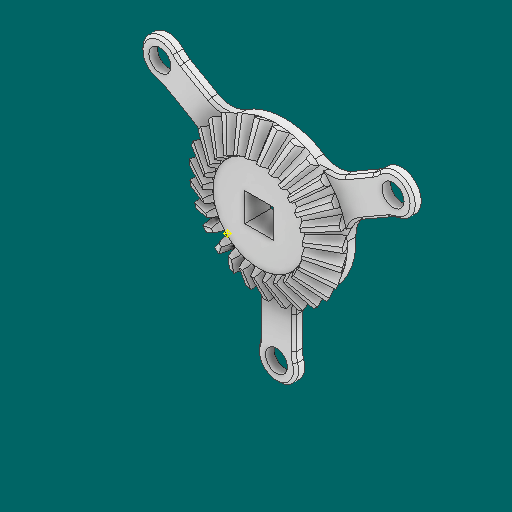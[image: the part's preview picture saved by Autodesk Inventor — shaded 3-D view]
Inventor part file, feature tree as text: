
AUTODESK INVENTOR PART (.ipt)
format: ipt  version: 2023.1 (Build 271208000, 208)  size: 768,512 bytes
history: native  units: mm
features: other x24, pattern_circular x3, sketch x3, loft x2, extrude x2, fillet x1, chamfer x1
ambient origin geometry x6: Origin, XZ Plane, X Axis, Y Axis, Z Axis, Center Point
bodies: Solid1 (feature_tree)
feature tree (36):
  other  "Top Point"
  other  "Mesh Plane2"
  other  "Teeth Body"
  other  "Start Point"
  other  "Tooth Plane"
  other  "Start Sketch"
  other  "End Point"
  other  "3D Sketch Right"
  other  "End Plane Right"
  loft  "Loft Right"
  pattern_circular  "Circular Pattern Right"  [2 undecoded]
  other  "3D Sketch Left"
  other  "End Plane Left"
  loft  "Loft Left"
  pattern_circular  "Circular Pattern Left"  [2 undecoded]
  other  "Fix Body"
  extrude  "Extrusion1"  Depth=5.08mm
  fillet  "Fillet1"  Radius=31.06566mm
  pattern_circular  "Circular Pattern4"  [2 undecoded]
  extrude  "Extrusion2"  Depth=5.08mm
  chamfer  "Chamfer1"  Distance=6.192895mm
  other  "Mesh Plane"
  other  "Top Plane"
  other  "Teeth Body Sketch"
  other  "End Plane"
  other  "End Sketch"
  other  "Helical Curve Left"
  other  "End Sketch Left"
  other  "Body Sketch"
  sketch  "Sketch6"  dims[d0=34.29mm d1=32.736122mm]
  other  "Srf1"
  other  "Helical Curve Right"
  other  "End Sketch Right"
  sketch  "Sketch8"  dims[d2=35.584898mm]
  sketch  "Sketch9"  dims[d3=6.985mm d4=9.06743mm d5=90.0deg d7=9.009874mm d8=9.638731mm d9=31.06566mm d11=7.1247mm d12=5.788854mm d15=6.192895mm d16=19.95972mm d17=0.0mm d18=90.0deg d19=0.0mm d20=90.0deg d21=270.0mm d22=360.0deg d26=144.697709mm d27=3.632189mm d28=34.29mm d29=-10.358413mm d30=5.788854mm d31=6.192895mm d32=19.95972mm d35=0.0mm d37=0.0mm d39=0.0mm d40=90.0deg d41=270.0mm d42=360.0deg d46=90.0deg d47=90.0deg d48=0.0mm d49=0.0mm d50=90.0deg d51=1.163553mm d52=0.0mm d53=0.0mm d54=0.0mm d56=5.887559mm d57=35.738878mm d58=31.771398mm d59=22.962267mm d60=20.413157mm d61=22.962267mm d62=20.413157mm d63=90.0deg d64=90.0deg d65=144.697709mm d66=31.5mm d67=34.29mm d68=-10.358413mm d69=3.632189mm d70=6.192895mm d71=19.95972mm d72=5.788854mm d73=20.413157mm d74=22.962267mm d75=0.0mm d76=90.0deg d77=0.0mm d78=90.0deg d79=0.0mm d80=90.0deg d81=270.0mm d82=360.0deg d84=10.0mm d85=20.0mm d86=20.0mm d87=10.0mm d88=0.0mm d89=0.0mm d90=5.08mm d91=62.23mm d92=30.0mm d94=360.0deg d96=2.0mm d97=7.9375mm d98=30.0mm d100=360.0deg d102=2.0mm d103=0.0mm d104=6.35mm d105=30.0mm d106=360.0deg d108=6.604mm d109=6.604mm d110=0.0mm d111=0.0mm d112=0.6mm d113=3.175mm d114=45.0deg]
  other  "Pitch Diameter"
note: 6 required parameter values undecoded (feature->parameter linkage not recoverable at this tier; creation-order binding heuristic only, values carry confidence <= 0.55)
